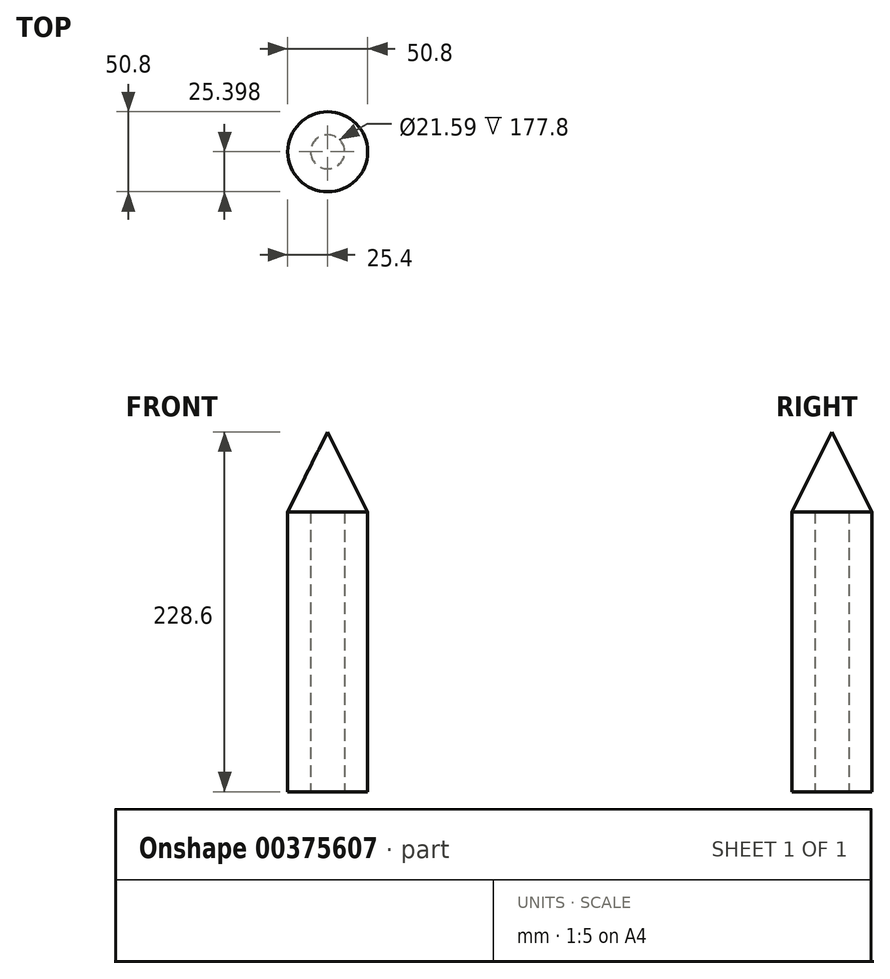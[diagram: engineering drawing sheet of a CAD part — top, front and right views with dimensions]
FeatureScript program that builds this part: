
annotation { "Feature Type Name" : "Feature", "Feature Type Description" : "" }
export const myFeature = defineFeature(function(context is Context, id is Id, definition is map)
    precondition{}
    {
        {
            var Q0;
            Q0=qCreatedBy(makeId("Top.planeOp"),FACE);
            var sketch = newSketch(context, id + "F0", { "sketchPlane" : qUnion([Q0])});
            skCircle(sketch, "E0", {"center": v(0, -4.2) * mm, "radius": 25.4 * mm});
            skCircle(sketch, "E1", {"center": v(0, -4.2) * mm, "radius": 10.8 * mm});
            skSolve(sketch);
        }
        {
            var Q0;
            Q0=makeQuery(id+"F0.imprint","IMPRINT",FACE,{"disambiguationData":[TD([[makeQuery(id+"F0.imprint","IMPRINT",EDGE,{"derivedFrom":sQuery(id+"F0.wireOp",EDGE,"E0")}),1.0]])]});
            extrude(context, id + "F1", {"entities" : qUnion([Q0]), "depth" : 177.8 * mm});
        }
        {
            var Q0;
            Q0=makeQuery(id+"F1.opExtrude","CAP_FACE",FACE,{"disambiguationData":[OSD([sQuery(id+"F0.wireOp",EDGE,"E0"),sQuery(id+"F0.wireOp",EDGE,"E1")])],"isStart":false});
            var sketch = newSketch(context, id + "F2", { "sketchPlane" : qUnion([Q0])});
            skCircle(sketch, "E2", {"center": v(0, -4.2) * mm, "radius": 25.4 * mm});
            skSolve(sketch);
        }
        {
            var Q0;
            Q0=qSketchRegion(id+"F2",true);
            extrude(context, id + "F3", {"entities" : qUnion([Q0]), "operationType" : NewBodyOperationType.ADD, "depth" : 50.8 * mm});
        }
        {
            var Q0;
            Q0=makeQuery(id+"F3.opExtrude","CAP_FACE",FACE,{"disambiguationData":[OSD([sQuery(id+"F2.wireOp",EDGE,"E2")])],"isStart":false});
            chamfer(context, id + "F4", {"entities" : qUnion([Q0]), "chamferType" : ChamferType.TWO_OFFSETS, "width1" : 50.8 * mm, "oppositeDirection" : true, "width2" : 25.4 * mm, "tangentPropagation" : true});
        }
    });
